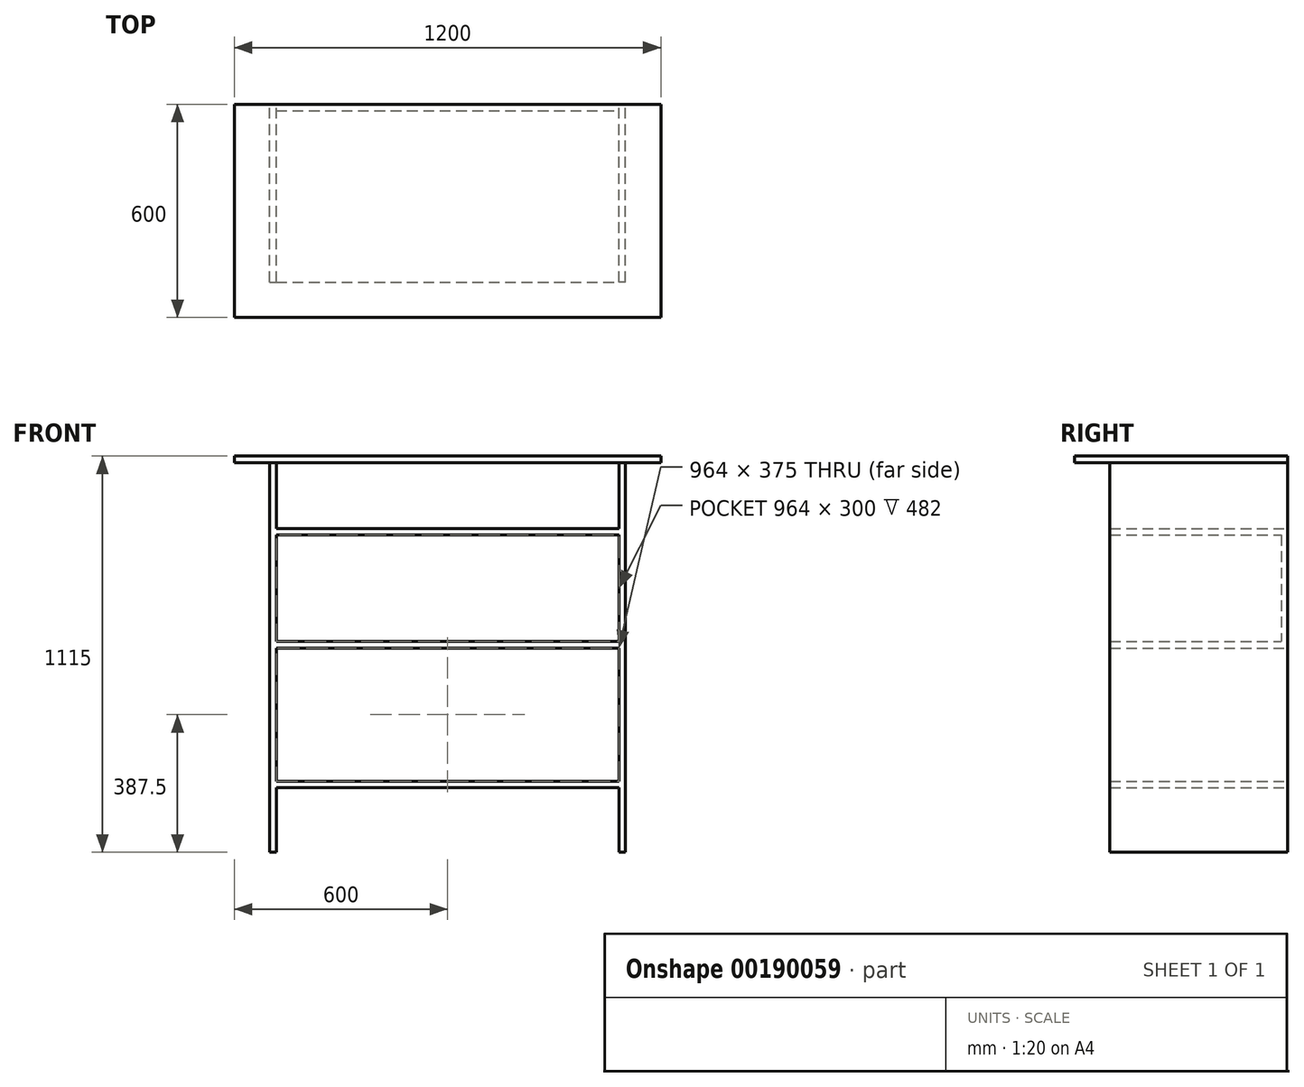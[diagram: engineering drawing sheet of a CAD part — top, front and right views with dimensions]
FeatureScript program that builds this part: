
annotation { "Feature Type Name" : "Feature", "Feature Type Description" : "" }
export const myFeature = defineFeature(function(context is Context, id is Id, definition is map)
    precondition{}
    {
        {
            var Q0;
            Q0=qCreatedBy(makeId("Front.planeOp"),FACE);
            var sketch = newSketch(context, id + "F0", { "sketchPlane" : qUnion([Q0])});
            skLineSegment(sketch, "E0.bottom", {"start": v(-600, 1115) * mm, "end": v(600, 1115) * mm});
            skLineSegment(sketch, "E0.top", {"start": v(-600, 1097) * mm, "end": v(600, 1097) * mm});
            skLineSegment(sketch, "E0.left", {"start": v(-600, 1115) * mm, "end": v(-600, 1097) * mm});
            skLineSegment(sketch, "E0.right", {"start": v(600, 1115) * mm, "end": v(600, 1097) * mm});
            skLineSegment(sketch, "E1", {"start": v(0, 0) * mm, "end": v(0, 1097) * mm, "construction": true});
            skSolve(sketch);
        }
        {
            var Q0;
            Q0 = qSketchRegion(id + "F0", true);
            extrude(context, id + "F1", {"entities" : qUnion([Q0]), "depth" : 600 * mm});
        }
        {
            var Q0;
            Q0=qCreatedBy(makeId("Front.planeOp"),FACE);
            var sketch = newSketch(context, id + "F2", { "sketchPlane" : qUnion([Q0])});
            skLineSegment(sketch, "E2.bottom", {"start": v(-500, 1097) * mm, "end": v(-482, 1097) * mm});
            skLineSegment(sketch, "E2.top", {"start": v(-500, 0) * mm, "end": v(-482, 0) * mm});
            skLineSegment(sketch, "E2.left", {"start": v(-500, 1097) * mm, "end": v(-500, 0) * mm});
            skLineSegment(sketch, "E2.right", {"start": v(-482, 1097) * mm, "end": v(-482, 0) * mm});
            skLineSegment(sketch, "E3", {"start": v(-482, 0) * mm, "end": v(0, 0) * mm, "construction": true});
            skLineSegment(sketch, "E4.MirrorCS", {"start": v(500, 1097) * mm, "end": v(482, 1097) * mm});
            skLineSegment(sketch, "E5.MirrorCS", {"start": v(482, 1097) * mm, "end": v(482, 0) * mm});
            skLineSegment(sketch, "E6.MirrorCS", {"start": v(500, 1097) * mm, "end": v(500, 0) * mm});
            skLineSegment(sketch, "E7.MirrorCS", {"start": v(500, 0) * mm, "end": v(482, 0) * mm});
            skSolve(sketch);
        }
        {
            var Q0;
            Q0 = qSketchRegion(id + "F2", true);
            extrude(context, id + "F3", {"entities" : qUnion([Q0]), "operationType" : NewBodyOperationType.ADD, "depth" : 500 * mm});
        }
        {
            var Q0;
            Q0=qCreatedBy(makeId("Front.planeOp"),FACE);
            var sketch = newSketch(context, id + "F4", { "sketchPlane" : qUnion([Q0])});
            skLineSegment(sketch, "E8.bottom", {"start": v(-482, 200) * mm, "end": v(482, 200) * mm});
            skLineSegment(sketch, "E8.top", {"start": v(-482, 182) * mm, "end": v(482, 182) * mm});
            skLineSegment(sketch, "E8.left", {"start": v(-482, 200) * mm, "end": v(-482, 182) * mm});
            skLineSegment(sketch, "E8.right", {"start": v(482, 200) * mm, "end": v(482, 182) * mm});
            skLineSegment(sketch, "E9.bottom", {"start": v(-482, 575) * mm, "end": v(482, 575) * mm});
            skLineSegment(sketch, "E9.top", {"start": v(-482, 593) * mm, "end": v(482, 593) * mm});
            skLineSegment(sketch, "E9.left", {"start": v(-482, 575) * mm, "end": v(-482, 593) * mm});
            skLineSegment(sketch, "E9.right", {"start": v(482, 575) * mm, "end": v(482, 593) * mm});
            skLineSegment(sketch, "E10.bottom", {"start": v(-482, 893) * mm, "end": v(482, 893) * mm});
            skLineSegment(sketch, "E10.top", {"start": v(-482, 911) * mm, "end": v(482, 911) * mm});
            skLineSegment(sketch, "E10.left", {"start": v(-482, 893) * mm, "end": v(-482, 911) * mm});
            skLineSegment(sketch, "E10.right", {"start": v(482, 893) * mm, "end": v(482, 911) * mm});
            skSolve(sketch);
        }
        {
            var Q0;
            Q0 = qSketchRegion(id + "F4", true);
            extrude(context, id + "F5", {"entities" : qUnion([Q0]), "operationType" : NewBodyOperationType.ADD, "depth" : 500 * mm});
        }
        {
            var Q0;
            Q0=qCreatedBy(makeId("Front.planeOp"),FACE);
            var sketch = newSketch(context, id + "F6", { "sketchPlane" : qUnion([Q0])});
            skLineSegment(sketch, "E11.bottom", {"start": v(-482, 893) * mm, "end": v(482, 893) * mm});
            skLineSegment(sketch, "E11.top", {"start": v(-482, 593) * mm, "end": v(482, 593) * mm});
            skLineSegment(sketch, "E11.left", {"start": v(-482, 893) * mm, "end": v(-482, 593) * mm});
            skLineSegment(sketch, "E11.right", {"start": v(482, 893) * mm, "end": v(482, 593) * mm});
            skSolve(sketch);
        }
        {
            var Q0;
            Q0 = qSketchRegion(id + "F6", true);
            extrude(context, id + "F7", {"entities" : qUnion([Q0]), "operationType" : NewBodyOperationType.ADD, "depth" : 18 * mm});
        }
    });
